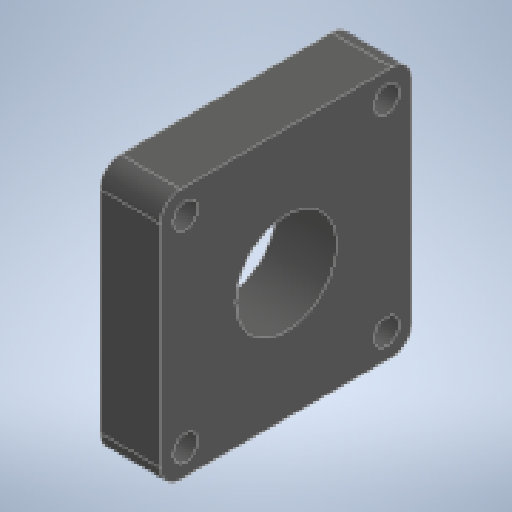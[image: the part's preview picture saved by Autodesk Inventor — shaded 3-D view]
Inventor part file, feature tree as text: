
AUTODESK INVENTOR PART (.ipt)
format: ipt  version: 2024.1 (Build 281209000, 209)  size: 237,568 bytes
history: native  units: in
note: dims shown in document units (in); Inventor stores cm internally (conversion verified against a paired STEP export)
features: extrude x3, sketch x3, fillet x1
ambient origin geometry x8: Origin, YZ Plane, XZ Plane, XY Plane, X Axis, Y Axis, Z Axis, Center Point
bodies: Solid1 (feature_tree)
feature tree (7):
  extrude  "Extrusion1"  Depth=0.9843in
  fillet  "Fillet1"  Radius=0.2362in
  extrude  "Extrusion2"  Depth=0.0787in
  extrude  "Extrusion3"  Depth=0.3937in
  sketch  "Sketch1"  dims[d0=0.9843in d1=0.9843in d2=0.2362in d3=0.0in]
  sketch  "Sketch2"  dims[d4=0.0787in d5=0.0984in]
  sketch  "Sketch3"  dims[d6=0.0984in d7=0.0984in d8=0.0984in d9=0.0984in d10=0.0984in d11=0.0984in d12=0.0984in d13=0.0984in d14=0.0984in d15=0.0984in d16=0.0984in d17=0.0in d18=0.0in d19=0.3937in d20=0.4921in d21=0.4921in d22=0.3937in d23=0.0in]
